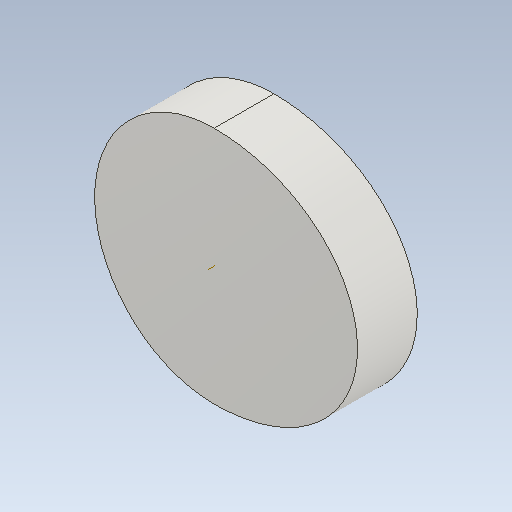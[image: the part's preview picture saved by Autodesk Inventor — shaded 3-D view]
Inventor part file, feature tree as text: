
AUTODESK INVENTOR PART (.ipt)
format: ipt  version: 2021.1 (Build 251245000, 245)  size: 97,792 bytes
history: native  units: mm (DEFAULTED — no unit token found)
features: extrude x1, other x1
ambient origin geometry x8: Origin, YZ Plane, XZ Plane, XY Plane, X Axis, Y Axis, Z Axis, Center Point
bodies: Solid1 (feature_tree)
feature tree (2):
  extrude  "Cam"  TaperAngle=0.0deg  [1 undecoded]
  other  "Main Sketch"
note: 1 required parameter value undecoded (feature->parameter linkage not recoverable at this tier; creation-order binding heuristic only, values carry confidence <= 0.55)
